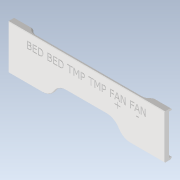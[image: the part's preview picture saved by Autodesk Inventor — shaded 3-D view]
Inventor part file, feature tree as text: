
AUTODESK INVENTOR PART (.ipt)
format: ipt  version: 2022.1 (Build 261234020, 234B)  size: 589,824 bytes
history: native  units: mm
features: reference x9, sketch x6, extrude x5, chamfer x4, other x4, fillet x2, projected_geometry x2
ambient origin geometry x8: Origin, YZ Plane, XZ Plane, XY Plane, X Axis, Y Axis, Z Axis, Center Point
bodies: Volumenkörper1 (feature_tree)
feature tree (32):
  extrude  "Extrusion1"  Depth=0.4mm
  extrude  "Extrusion2"  Depth=2.0mm
  extrude  "Extrusion3"  Depth=0.4mm
  extrude  "Extrusion4"  Depth=0.4mm
  chamfer  "Fase1"  Distance=2.0mm
  fillet  "Rundung1"  Radius=3.4mm
  chamfer  "Fase3"  Distance=3.0mm
  extrude  "Extrusion5"  TaperAngle=0.0deg  [1 undecoded]
  fillet  "Rundung2"  Radius=4.0mm
  chamfer  "Fase5"  Distance=0.4mm Angle=45.0deg
  chamfer  "Fase6"  Distance=10.0mm
  other  "Prägen1"
  sketch  "Skizze1"  dims[d0=0.4mm d1=0.4mm]
  reference  "Referenz1"
  reference  "Referenz2"
  sketch  "Skizze2"  dims[d2=2.0mm d3=2.0mm]
  projected_geometry  "Projizierte Kontur1"
  sketch  "Skizze3"  dims[d5=0.4mm d6=0.4mm]
  reference  "Referenz3"
  reference  "Referenz4"
  reference  "Referenz5"
  reference  "Referenz6"
  sketch  "Skizze4"  dims[d7=0.4mm d8=0.4mm d9=2.0mm d10=0.0mm d11=3.4mm d12=0.0mm d13=3.0mm d14=0.0mm]
  projected_geometry  "Projizierte Kontur2"
  reference  "Referenz7"
  reference  "Referenz8"
  sketch  "Skizze5"  dims[d15=2.4mm d16=0.0mm d17=0.0mm]
  sketch  "Skizze6"  dims[d18=3.0mm d19=2.0mm d20=45.0deg d21=4.0mm d25=0.4mm d26=2.0mm d27=45.0deg d31=10.0mm d32=50.0mm d33=0.0mm d34=0.0mm d35=10.0mm d36=0.4mm d37=2.0mm d38=45.0deg d39=1.0mm d40=2.0mm d41=45.0deg d44=5.0mm d45=12.0mm d46=5.0mm d47=5.0mm d48=0.0mm d49=0.0mm d50=5.0mm d51=0.0mm d52=1.4mm d53=0.0mm]
  reference  "Referenz9"
  other  "<userpath>\Desktop\RAMA_SBNG\BedPan\Ramabed.iam"
  other  "Ramabed.iam"
  other  "Ramabed wago mount:1"
note: 1 required parameter value undecoded (feature->parameter linkage not recoverable at this tier; creation-order binding heuristic only, values carry confidence <= 0.55)
